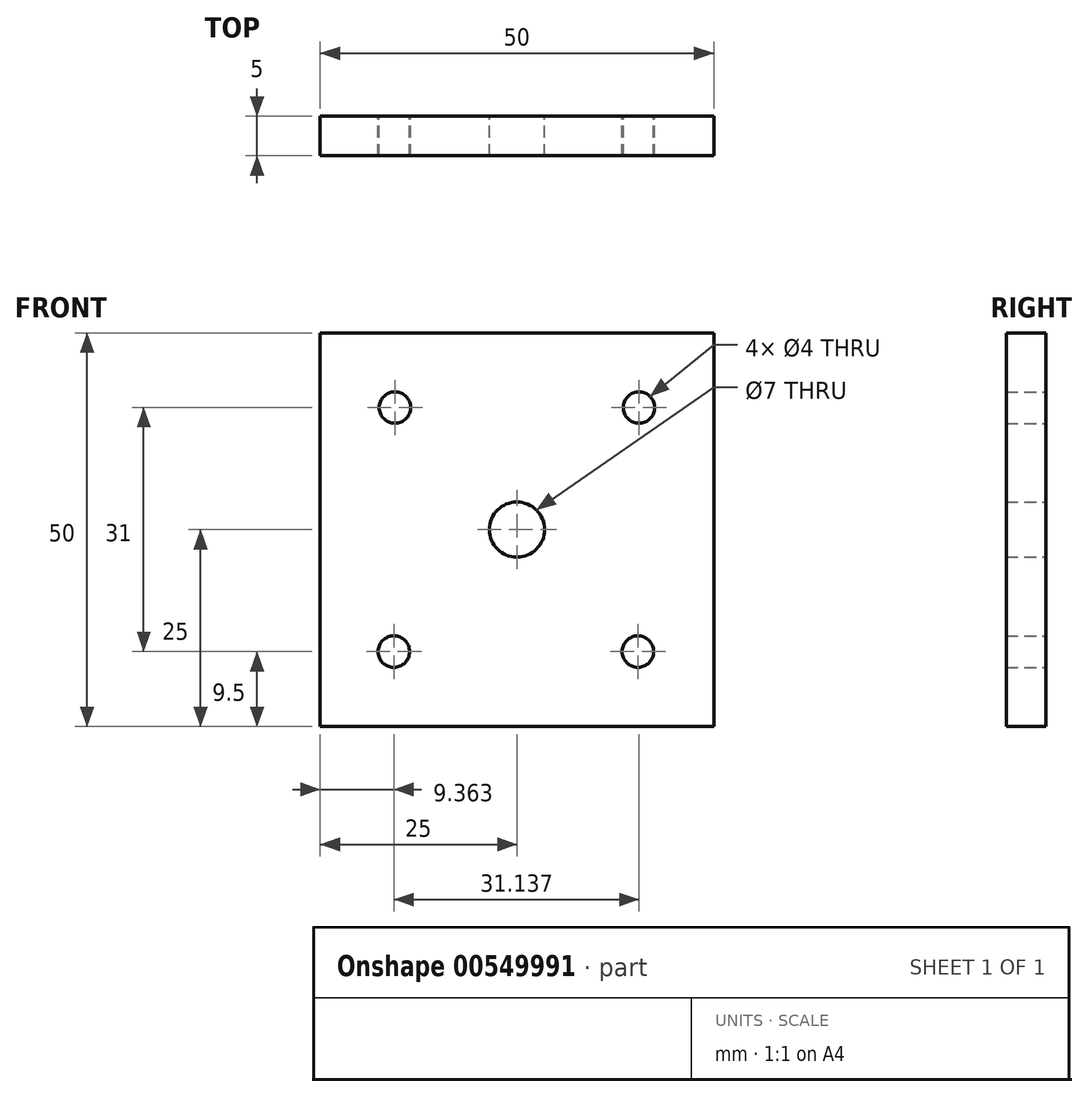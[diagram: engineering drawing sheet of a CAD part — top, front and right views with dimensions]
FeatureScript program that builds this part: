
annotation { "Feature Type Name" : "Feature", "Feature Type Description" : "" }
export const myFeature = defineFeature(function(context is Context, id is Id, definition is map)
    precondition{}
    {
        {
            var Q0;
            Q0=qCreatedBy(makeId("Front.planeOp"),FACE);
            var sketch = newSketch(context, id + "F0", { "sketchPlane" : qUnion([Q0])});
            skLineSegment(sketch, "E0.bottom", {"start": v(25, -25) * mm, "end": v(-25, -25) * mm});
            skLineSegment(sketch, "E0.top", {"start": v(25, 25) * mm, "end": v(-25, 25) * mm});
            skLineSegment(sketch, "E0.left", {"start": v(25, -25) * mm, "end": v(25, 25) * mm});
            skLineSegment(sketch, "E0.right", {"start": v(-25, -25) * mm, "end": v(-25, 25) * mm});
            skPoint(sketch, "E0.middle", {"position": v(0, 0) * mm});
            skCircle(sketch, "E1", {"center": v(-15.5, 15.5) * mm, "radius": 2 * mm});
            skCircle(sketch, "E2", {"center": v(15.5, 15.5) * mm, "radius": 2 * mm});
            skCircle(sketch, "E3", {"center": v(-15.64, -15.5) * mm, "radius": 2 * mm});
            skCircle(sketch, "E4", {"center": v(15.36, -15.5) * mm, "radius": 2 * mm});
            skCircle(sketch, "E5", {"center": v(0, 0) * mm, "radius": 3.5 * mm});
            skSolve(sketch);
        }
        {
            var Q0;
            Q0=makeQuery(id+"F0.imprint","IMPRINT",FACE,{"disambiguationData":[TD([[makeQuery(id+"F0.imprint","IMPRINT",EDGE,{"derivedFrom":sQuery(id+"F0.wireOp",EDGE,"E0.bottom")}),-1.0]])]});
            extrude(context, id + "F1", {"entities" : qUnion([Q0]), "depth" : 5 * mm, "offsetDistance" : 25 * mm});
        }
    });
